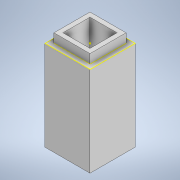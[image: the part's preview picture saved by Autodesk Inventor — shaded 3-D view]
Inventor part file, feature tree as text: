
AUTODESK INVENTOR PART (.ipt)
format: ipt  version: 2022 (Build 260153000, 153)  size: 120,832 bytes
history: native  units: in
note: dims shown in document units (in); Inventor stores cm internally (conversion verified against a paired STEP export)
features: sketch x3, extrude x2, projected_geometry x2, shell x1
ambient origin geometry x8: Origin, YZ Plane, XZ Plane, XY Plane, X Axis, Y Axis, Z Axis, Center Point
bodies: Solid1 (feature_tree)
feature tree (8):
  extrude  "Extrusion1"  Depth=0.1969in
  shell  "Shell1"  Thickness=0.3937in
  extrude  "Extrusion2"  Depth=0.0197in
  sketch  "Sketch3"  dims[d6=0.0394in d7=0.0in]
  sketch  "Sketch1"  dims[d0=0.1969in d1=0.1969in d2=0.3937in d3=0.0in]
  sketch  "Sketch2"  dims[d4=0.0394in d5=0.0197in]
  projected_geometry  "Projected Loop1"
  projected_geometry  "Projected Loop2"
